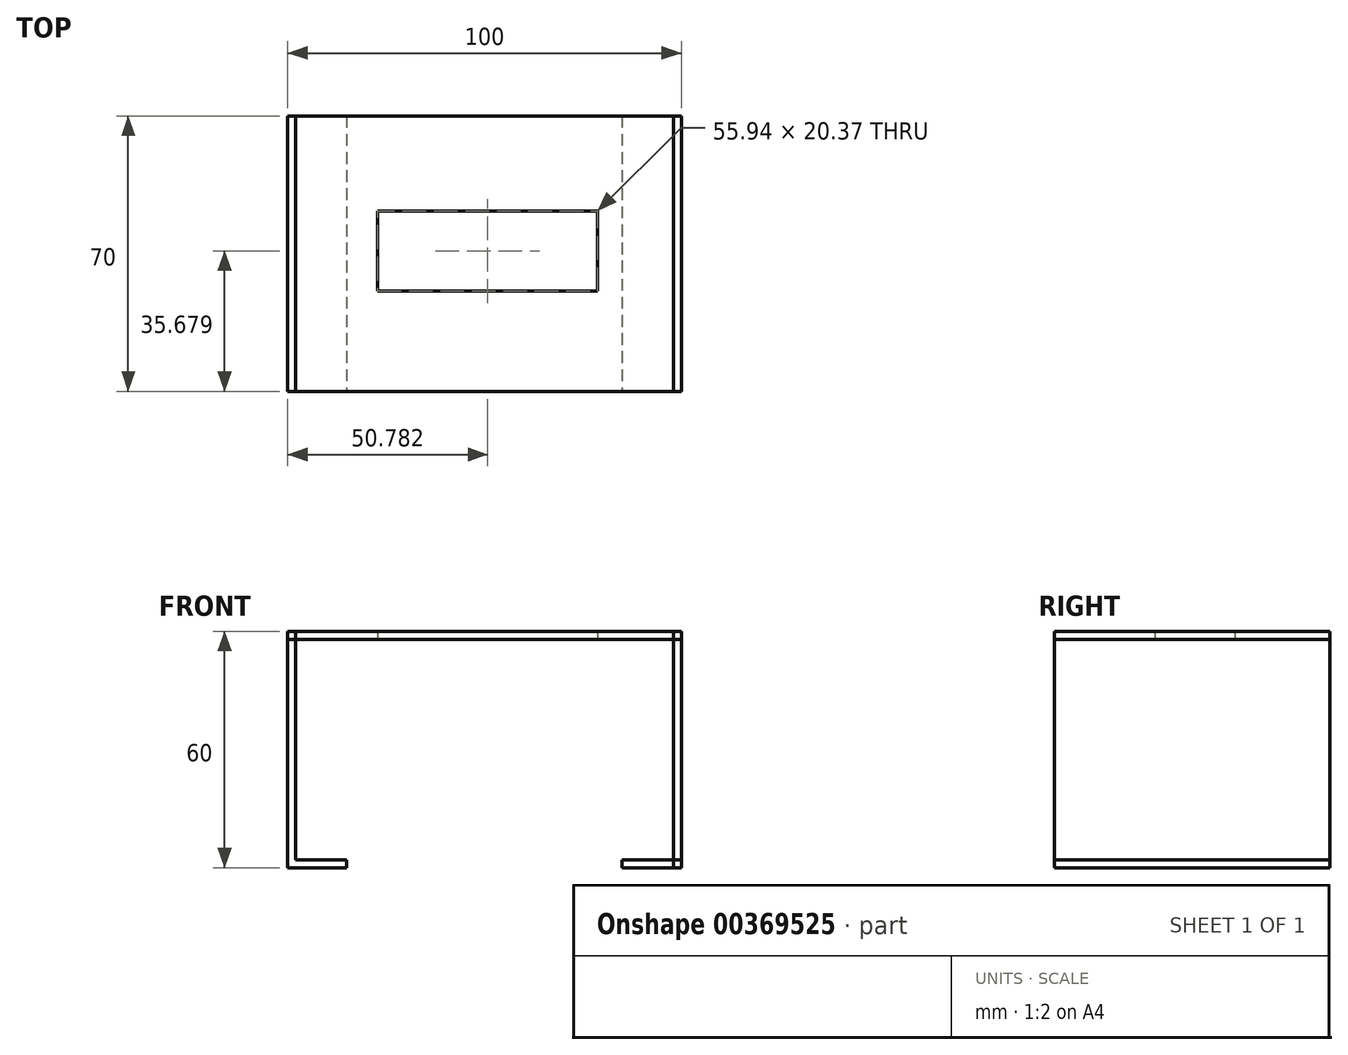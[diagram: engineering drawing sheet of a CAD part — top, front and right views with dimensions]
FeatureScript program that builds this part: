
annotation { "Feature Type Name" : "Feature", "Feature Type Description" : "" }
export const myFeature = defineFeature(function(context is Context, id is Id, definition is map)
    precondition{}
    {
        {
            var Q0;
            Q0=qCreatedBy(makeId("Front.planeOp"),FACE);
            var sketch = newSketch(context, id + "F0", { "sketchPlane" : qUnion([Q0])});
            skLineSegment(sketch, "E0", {"start": v(-37.14, -29.05) * mm, "end": v(-52.14, -29.05) * mm});
            skLineSegment(sketch, "E1", {"start": v(-52.14, -29.05) * mm, "end": v(-52.14, 30.95) * mm});
            skLineSegment(sketch, "E2", {"start": v(-52.14, 30.95) * mm, "end": v(47.86, 30.95) * mm});
            skLineSegment(sketch, "E3", {"start": v(47.86, 30.95) * mm, "end": v(47.86, -29.05) * mm});
            skLineSegment(sketch, "E4", {"start": v(47.86, -29.05) * mm, "end": v(32.86, -29.05) * mm});
            skSolve(sketch);
        }
        {
            var Q0;
            Q0=sQuery(id+"F0.wireOp",EDGE,"E2");
            var Q1;
            Q1=sQuery(id+"F0.wireOp",EDGE,"E3");
            var Q2;
            Q2=sQuery(id+"F0.wireOp",EDGE,"E0");
            var Q3;
            Q3=sQuery(id+"F0.wireOp",EDGE,"E1");
            var Q4;
            Q4=sQuery(id+"F0.wireOp",EDGE,"E4");
            extrude(context, id + "F1", {"bodyType" : ToolBodyType.SURFACE, "surfaceEntities" : qUnion([Q0, Q1, Q2, Q3, Q4]), "endBound" : BoundingType.SYMMETRIC, "depth" : 70 * mm});
        }
        {
            var Q0;
            Q0=makeQuery(id+"F1.opExtrude","SWEPT_FACE",FACE,{"disambiguationData":[OSD([sQuery(id+"F0.wireOp",EDGE,"E0")])]});
            var Q1;
            Q1=makeQuery(id+"F1.opExtrude","SWEPT_FACE",FACE,{"disambiguationData":[OSD([sQuery(id+"F0.wireOp",EDGE,"E4")])]});
            extrude(context, id + "F2", {"entities" : qUnion([Q0, Q1]), "depth" : 2 * mm});
        }
        {
            var Q0;
            Q0=makeQuery(id+"F1.opExtrude","SWEPT_FACE",FACE,{"disambiguationData":[OSD([sQuery(id+"F0.wireOp",EDGE,"E1")])]});
            extrude(context, id + "F3", {"entities" : qUnion([Q0]), "operationType" : NewBodyOperationType.ADD, "depth" : 2 * mm});
        }
        {
            var Q0;
            Q0=makeQuery(id+"F1.opExtrude","SWEPT_FACE",FACE,{"disambiguationData":[OSD([sQuery(id+"F0.wireOp",EDGE,"E2")])]});
            extrude(context, id + "F4", {"entities" : qUnion([Q0]), "depth" : 2 * mm});
        }
        {
            var Q0;
            Q0 = qSketchRegion(id + "F0", true);
            var Q1;
            Q1=makeQuery(id+"F1.opExtrude","SWEPT_FACE",FACE,{"disambiguationData":[OSD([sQuery(id+"F0.wireOp",EDGE,"E3")])]});
            extrude(context, id + "F5", {"entities" : qUnion([Q0, Q1]), "depth" : 2 * mm});
        }
        {
            var Q0;
            Q0=qCreatedBy(makeId("Top.planeOp"),FACE);
            var sketch = newSketch(context, id + "F6", { "sketchPlane" : qUnion([Q0])});
            skLineSegment(sketch, "E5.bottom", {"start": v(-29.33, 10.86) * mm, "end": v(26.61, 10.86) * mm});
            skLineSegment(sketch, "E5.top", {"start": v(-29.33, -9.5) * mm, "end": v(26.61, -9.5) * mm});
            skLineSegment(sketch, "E5.left", {"start": v(-29.33, 10.86) * mm, "end": v(-29.33, -9.5) * mm});
            skLineSegment(sketch, "E5.right", {"start": v(26.61, 10.86) * mm, "end": v(26.61, -9.5) * mm});
            skSolve(sketch);
        }
        {
            var Q0;
            Q0=makeQuery(id+"F6.imprint","IMPRINT",FACE,{"disambiguationData":[TD([[makeQuery(id+"F6.imprint","IMPRINT",EDGE,{"derivedFrom":sQuery(id+"F6.wireOp",EDGE,"E5.bottom")}),-1.0]])]});
            extrude(context, id + "F7", {"entities" : qUnion([Q0]), "operationType" : NewBodyOperationType.REMOVE, "endBound" : BoundingType.THROUGH_ALL, "depth" : 50 * mm});
        }
    });
